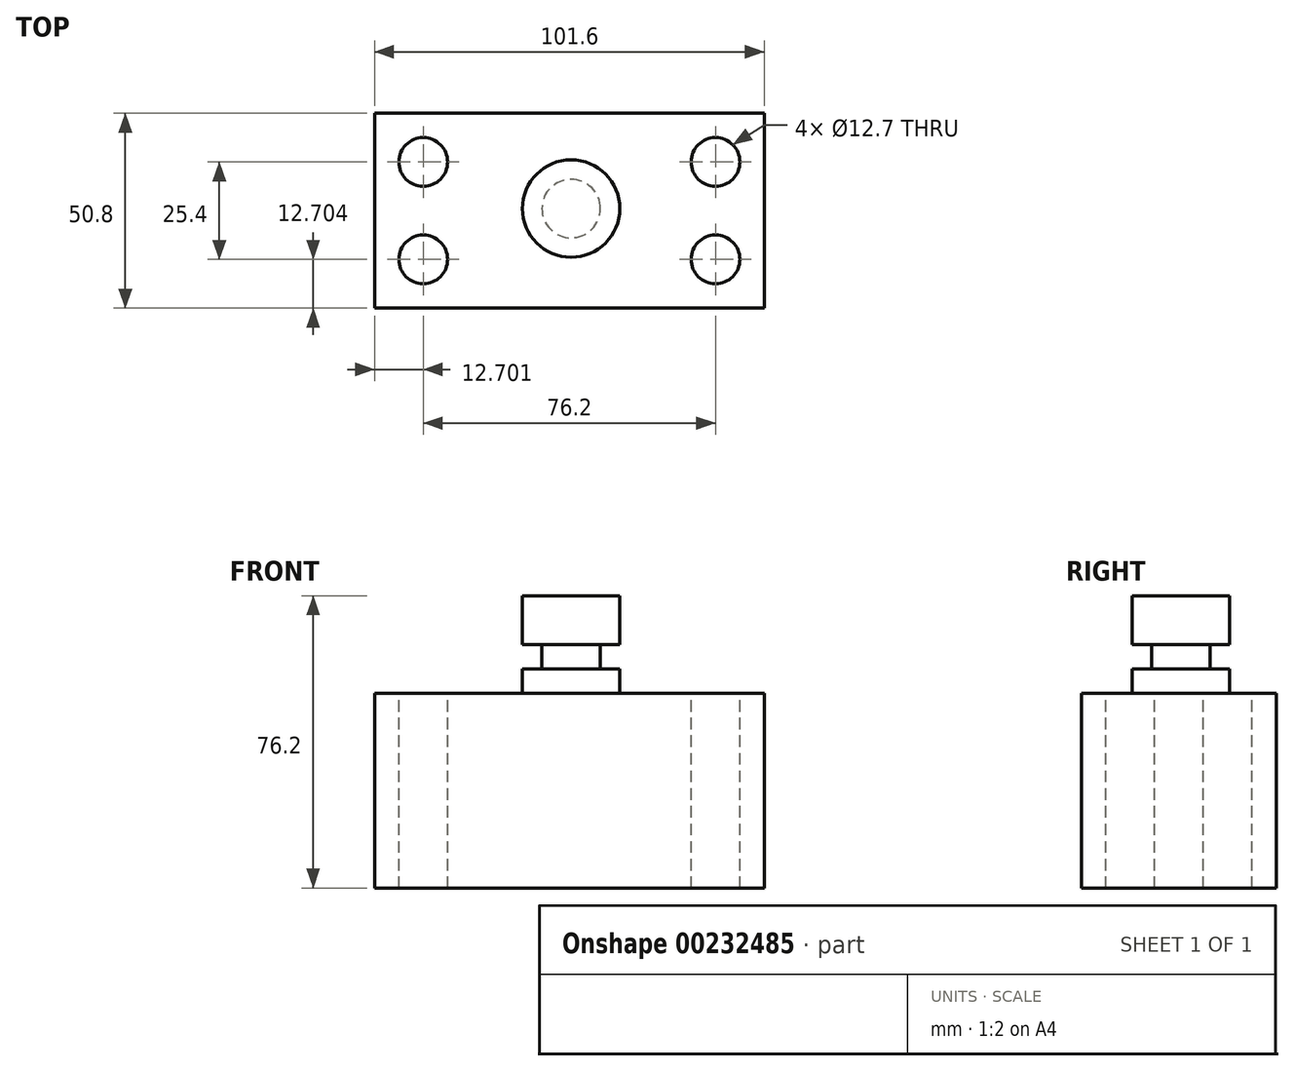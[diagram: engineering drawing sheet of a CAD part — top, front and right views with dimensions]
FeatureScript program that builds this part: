
annotation { "Feature Type Name" : "Feature", "Feature Type Description" : "" }
export const myFeature = defineFeature(function(context is Context, id is Id, definition is map)
    precondition{}
    {
        {
            var Q0;
            Q0=qCreatedBy(makeId("Top.planeOp"),FACE);
            var sketch = newSketch(context, id + "F0", { "sketchPlane" : qUnion([Q0])});
            skLineSegment(sketch, "E0.bottom", {"start": v(-51.27, 24.84) * mm, "end": v(50.33, 24.84) * mm});
            skLineSegment(sketch, "E0.top", {"start": v(-51.27, -25.96) * mm, "end": v(50.33, -25.96) * mm});
            skLineSegment(sketch, "E0.left", {"start": v(-51.27, 24.84) * mm, "end": v(-51.27, -25.96) * mm});
            skLineSegment(sketch, "E0.right", {"start": v(50.33, 24.84) * mm, "end": v(50.33, -25.96) * mm});
            skSolve(sketch);
        }
        {
            var Q0;
            Q0 = qSketchRegion(id + "F0", true);
            extrude(context, id + "F1", {"entities" : qUnion([Q0]), "depth" : 50.8 * mm});
        }
        {
            var Q0;
            Q0=makeQuery(id+"F1.opExtrude","CAP_FACE",FACE,{"disambiguationData":[OSD([sQuery(id+"F0.wireOp",EDGE,"E0.bottom"),sQuery(id+"F0.wireOp",EDGE,"E0.top"),sQuery(id+"F0.wireOp",EDGE,"E0.left"),sQuery(id+"F0.wireOp",EDGE,"E0.right")])],"isStart":false});
            var sketch = newSketch(context, id + "F2", { "sketchPlane" : qUnion([Q0])});
            skCircle(sketch, "E1", {"center": v(-38.57, 12.14) * mm, "radius": 6.35 * mm});
            skCircle(sketch, "E2", {"center": v(37.63, 12.14) * mm, "radius": 6.35 * mm});
            skCircle(sketch, "E3", {"center": v(37.63, -13.26) * mm, "radius": 6.35 * mm});
            skCircle(sketch, "E4", {"center": v(-38.57, -13.26) * mm, "radius": 6.35 * mm});
            skSolve(sketch);
        }
        {
            var Q0;
            Q0=makeQuery(id+"F2.imprint","IMPRINT",FACE,{"disambiguationData":[TD([[makeQuery(id+"F2.imprint","IMPRINT",EDGE,{"derivedFrom":sQuery(id+"F2.wireOp",EDGE,"E1")}),1.0]])]});
            var Q1;
            Q1=makeQuery(id+"F2.imprint","IMPRINT",FACE,{"disambiguationData":[TD([[makeQuery(id+"F2.imprint","IMPRINT",EDGE,{"derivedFrom":sQuery(id+"F2.wireOp",EDGE,"E2")}),1.0]])]});
            var Q2;
            Q2=makeQuery(id+"F2.imprint","IMPRINT",FACE,{"disambiguationData":[TD([[makeQuery(id+"F2.imprint","IMPRINT",EDGE,{"derivedFrom":sQuery(id+"F2.wireOp",EDGE,"E3")}),1.0]])]});
            var Q3;
            Q3=makeQuery(id+"F2.imprint","IMPRINT",FACE,{"disambiguationData":[TD([[makeQuery(id+"F2.imprint","IMPRINT",EDGE,{"derivedFrom":sQuery(id+"F2.wireOp",EDGE,"E4")}),1.0]])]});
            extrude(context, id + "F3", {"entities" : qUnion([Q0, Q1, Q2, Q3]), "operationType" : NewBodyOperationType.REMOVE, "endBound" : BoundingType.THROUGH_ALL, "oppositeDirection" : true, "depth" : 25.4 * mm});
        }
        {
            var Q0;
            Q0=qCreatedBy(makeId("Front.planeOp"),FACE);
            var sketch = newSketch(context, id + "F4", { "sketchPlane" : qUnion([Q0])});
            skLineSegment(sketch, "E5.bottom", {"start": v(0, 0) * mm, "end": v(0, 0) * mm});
            skLineSegment(sketch, "E5.top", {"start": v(0, 76.2) * mm, "end": v(0, 76.2) * mm});
            skLineSegment(sketch, "E5.left", {"start": v(0, 0) * mm, "end": v(0, 76.2) * mm});
            skLineSegment(sketch, "E5.right", {"start": v(0, 0) * mm, "end": v(0, 76.2) * mm});
            skLineSegment(sketch, "E6.bottom", {"start": v(-12.7, 76.2) * mm, "end": v(0, 76.2) * mm});
            skLineSegment(sketch, "E6.top", {"start": v(-12.7, 50.8) * mm, "end": v(0, 50.8) * mm});
            skLineSegment(sketch, "E6.left", {"start": v(-12.7, 76.2) * mm, "end": v(-12.7, 50.8) * mm});
            skLineSegment(sketch, "E6.right", {"start": v(0, 76.2) * mm, "end": v(0, 50.8) * mm});
            skSolve(sketch);
        }
        {
            var Q0;
            Q0=makeQuery(id+"F4.imprint","IMPRINT",FACE,{"disambiguationData":[TD([[makeQuery(id+"F4.imprint","IMPRINT",EDGE,{"derivedFrom":sQuery(id+"F4.wireOp",EDGE,"E6.bottom")}),-1.0]])]});
            var Q1;
            Q1=sQuery(id+"F4.wireOp",EDGE,"E6.right");
            revolve(context, id + "F5", {"operationType" : NewBodyOperationType.ADD, "entities" : qUnion([Q0]), "axis" : qUnion([Q1]), "revolveType" : RevolveType.FULL});
        }
        {
            var Q0;
            Q0=qCreatedBy(makeId("Front.planeOp"),FACE);
            var sketch = newSketch(context, id + "F6", { "sketchPlane" : qUnion([Q0])});
            skLineSegment(sketch, "E7.bottom", {"start": v(-7.62, 57.15) * mm, "end": v(-27.54, 57.15) * mm});
            skLineSegment(sketch, "E7.top", {"start": v(-7.62, 63.5) * mm, "end": v(-27.54, 63.5) * mm});
            skLineSegment(sketch, "E7.left", {"start": v(-7.62, 57.15) * mm, "end": v(-7.62, 63.5) * mm});
            skLineSegment(sketch, "E7.right", {"start": v(-27.54, 57.15) * mm, "end": v(-27.54, 63.5) * mm});
            skSolve(sketch);
        }
        {
            var Q0;
            Q0=makeQuery(id+"F6.imprint","IMPRINT",FACE,{"disambiguationData":[TD([[makeQuery(id+"F6.imprint","IMPRINT",EDGE,{"derivedFrom":sQuery(id+"F6.wireOp",EDGE,"E7.bottom")}),-1.0]])]});
            var Q1;
            Q1=makeQuery(id+"F5.opRevolve","SWEPT_FACE",FACE,{"disambiguationData":[OSD([sQuery(id+"F4.wireOp",EDGE,"E6.left")])]});
            revolve(context, id + "F7", {"operationType" : NewBodyOperationType.REMOVE, "entities" : qUnion([Q0]), "axis" : qUnion([Q1]), "revolveType" : RevolveType.FULL, "oppositeDirection" : true});
        }
    });
